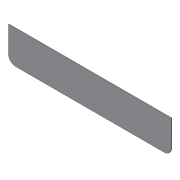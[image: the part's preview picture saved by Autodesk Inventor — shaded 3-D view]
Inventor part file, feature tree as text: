
AUTODESK INVENTOR PART (.ipt)
format: ipt  version: 2012 (Build 160160000, 160)  size: 68,096 bytes
history: native  units: in
note: dims shown in document units (in); Inventor stores cm internally (conversion verified against a paired STEP export)
features: extrude x1, sketch x1
ambient origin geometry x8: Origin, YZ Plane, XZ Plane, XY Plane, X Axis, Y Axis, Z Axis, Center Point
bodies: Solid1 (feature_tree)
feature tree (2):
  extrude  "Extrusion1"  Depth=14.0in
  sketch  "Sketch1"  dims[d0=69.0in d1=14.0in d2=3.0in d3=0.25in d4=0.0in]
